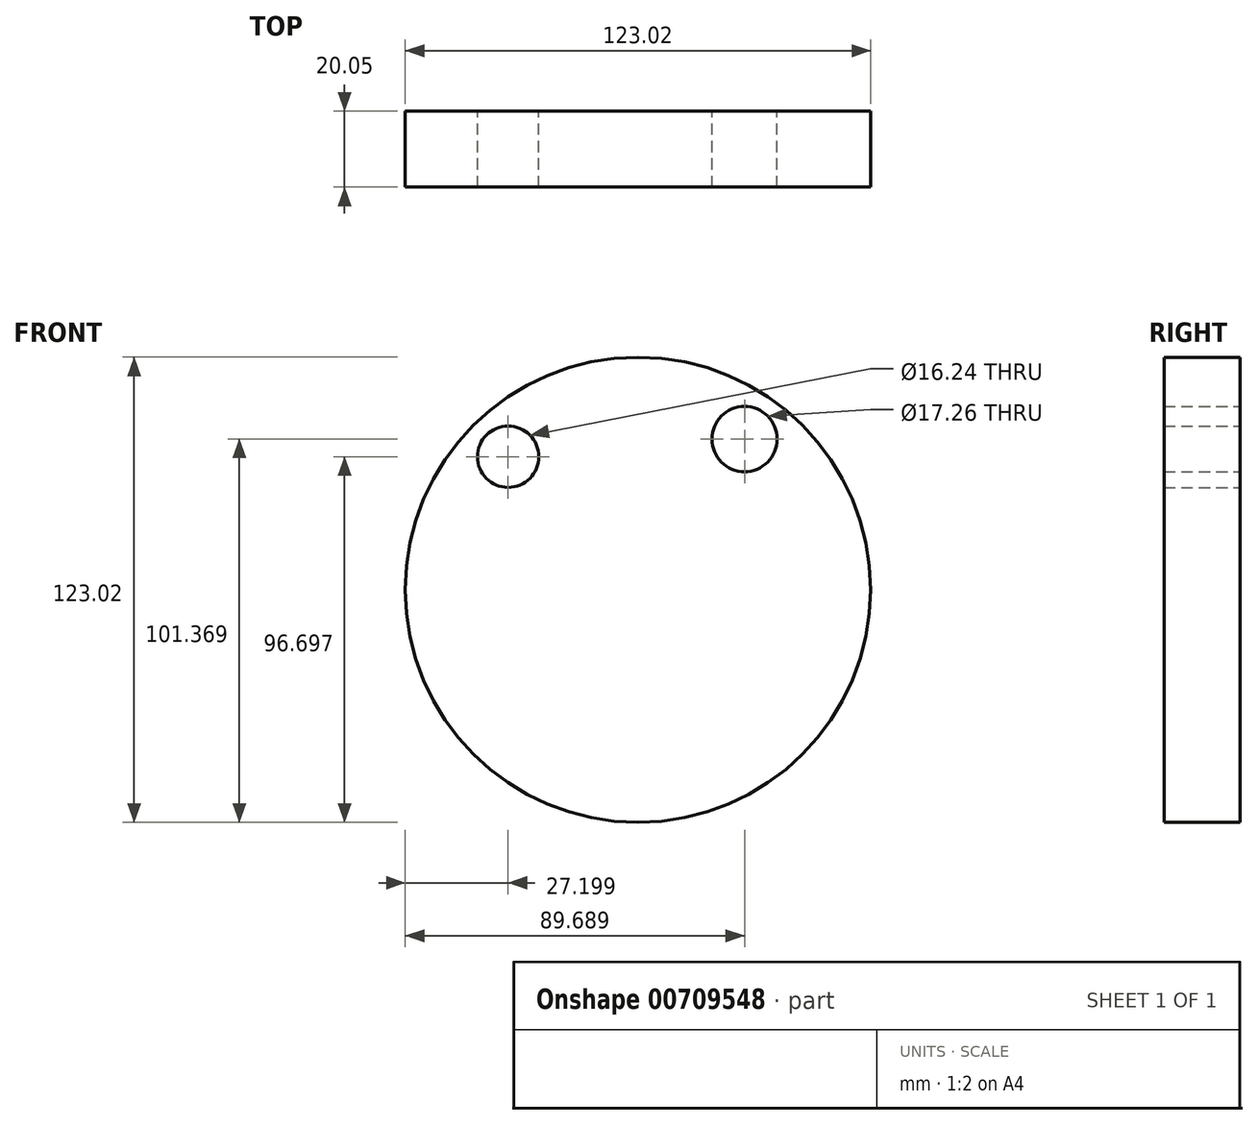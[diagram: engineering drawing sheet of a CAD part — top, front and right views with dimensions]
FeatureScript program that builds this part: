
annotation { "Feature Type Name" : "Feature", "Feature Type Description" : "" }
export const myFeature = defineFeature(function(context is Context, id is Id, definition is map)
    precondition{}
    {
        {
            var Q0;
            Q0=qCreatedBy(makeId("Front.planeOp"),FACE);
            var sketch = newSketch(context, id + "F0", { "sketchPlane" : qUnion([Q0])});
            skCircle(sketch, "E0", {"center": v(0, 0) * mm, "radius": 61.5 * mm});
            skCircle(sketch, "E1", {"center": v(-34.31, 35.19) * mm, "radius": 8.12 * mm});
            skCircle(sketch, "E2", {"center": v(28.18, 39.86) * mm, "radius": 8.63 * mm});
            skCircle(sketch, "E3", {"center": v(0, -24.97) * mm, "radius": 22.8 * mm});
            skSolve(sketch);
        }
        {
            var Q0;
            Q0=makeQuery(id+"F0.imprint","IMPRINT",FACE,{"disambiguationData":[TD([[makeQuery(id+"F0.imprint","IMPRINT",EDGE,{"derivedFrom":sQuery(id+"F0.wireOp",EDGE,"E0")}),1.0]])]});
            var Q1;
            Q1=makeQuery(id+"F0.imprint","IMPRINT",FACE,{"disambiguationData":[TD([[makeQuery(id+"F0.imprint","IMPRINT",EDGE,{"derivedFrom":sQuery(id+"F0.wireOp",EDGE,"E3")}),1.0]])]});
            extrude(context, id + "F1", {"entities" : qUnion([Q0, Q1]), "depth" : 20.05 * mm, "offsetDistance" : 25.4 * mm});
        }
    });
